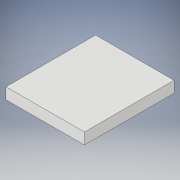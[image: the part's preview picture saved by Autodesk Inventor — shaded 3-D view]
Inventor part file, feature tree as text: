
AUTODESK INVENTOR PART (.ipt)
format: ipt  version: 2019 (Build 230136000, 136)  size: 231,936 bytes
history: native  units: in
note: dims shown in document units (in); Inventor stores cm internally (conversion verified against a paired STEP export)
features: extrude x5, sketch x5
ambient origin geometry x8: Origin, YZ Plane, XZ Plane, XY Plane, X Axis, Y Axis, Z Axis, Center Point
bodies: Solid1 (feature_tree)
feature tree (10):
  extrude  "Extrusion1"  Depth=6.2992in
  extrude  "Extrusion2"  Depth=3.1496in
  sketch  "Sketch3"  dims[d6=0.7874in d7=0.0in d8=3.937in]
  extrude  "Extrusion5"  Depth=0.7874in
  extrude  "Extrusion4"  Depth=0.3937in TaperAngle=0.0deg
  extrude  "Extrusion6"  Depth=0.7874in
  sketch  "Sketch1"  dims[d0=5.5118in d1=6.2992in]
  sketch  "Sketch2"  dims[d4=2.7559in d5=3.1496in]
  sketch  "Sketch4"  dims[d9=4.7244in d10=0.3937in d11=0.0in]
  sketch  "Sketch5"  dims[d12=0.7874in d13=0.7874in d14=0.7874in d15=0.7874in d16=0.7874in d17=0.7874in d18=0.7874in d19=0.7874in d20=0.7874in d21=0.7874in d22=0.7874in d23=0.7874in d25=0.7874in d26=0.7874in d27=0.7874in d28=0.7874in d29=0.7874in d30=0.7874in d31=0.7874in d32=0.7874in d33=0.7874in d34=0.7874in d35=0.7874in d36=0.7874in d37=0.7874in d38=0.7874in d39=0.7874in d40=0.7874in d41=0.7874in d42=0.7874in d43=0.7874in d44=0.7874in d45=0.7874in d46=0.7874in d47=0.7874in d48=0.7874in d49=0.7874in d50=0.7874in d53=0.1969in d54=0.1969in d55=0.1969in d56=0.1969in d57=4.7244in d58=3.5433in d63=0.4823in d73=0.1969in d75=0.3937in d76=0.0in d77=0.7874in d78=0.7874in d79=0.7874in d80=0.7874in d81=0.7874in d82=0.7874in d83=0.7874in d84=0.7874in d85=0.7874in d86=0.3937in d87=0.0in d88=0.1969in d90=0.1969in d91=0.3937in d92=0.0in]
